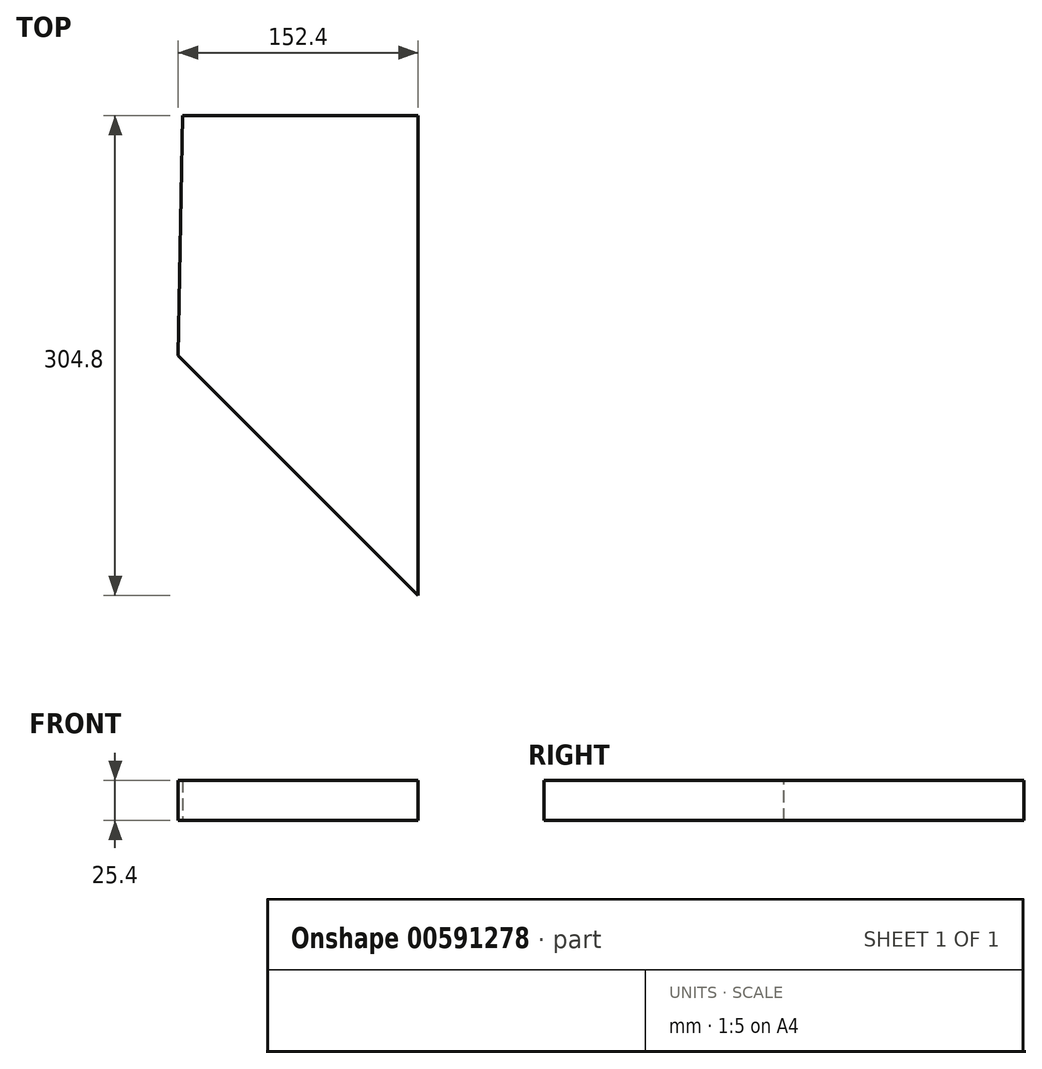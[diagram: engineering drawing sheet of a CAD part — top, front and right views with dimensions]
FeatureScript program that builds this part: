
annotation { "Feature Type Name" : "Feature", "Feature Type Description" : "" }
export const myFeature = defineFeature(function(context is Context, id is Id, definition is map)
    precondition{}
    {
        {
            var Q0;
            Q0=qCreatedBy(makeId("Top.planeOp"),FACE);
            var sketch = newSketch(context, id + "F0", { "sketchPlane" : qUnion([Q0])});
            skLineSegment(sketch, "E0.bottom", {"start": v(152.4, -152.4) * mm, "end": v(-152.4, -152.4) * mm});
            skLineSegment(sketch, "E0.top", {"start": v(152.4, 152.4) * mm, "end": v(-152.4, 152.4) * mm});
            skLineSegment(sketch, "E0.left", {"start": v(152.4, -152.4) * mm, "end": v(152.4, 152.4) * mm});
            skLineSegment(sketch, "E0.right", {"start": v(-152.4, -152.4) * mm, "end": v(-152.4, 152.4) * mm});
            skPoint(sketch, "E0.middle", {"position": v(0, 0) * mm});
            skSolve(sketch);
        }
        {
            var Q0;
            Q0 = qSketchRegion(id + "F0", true);
            extrude(context, id + "F1", {"entities" : qUnion([Q0]), "depth" : 25.4 * mm, "offsetDistance" : 25.4 * mm});
        }
        {
            var Q0;
            Q0=makeQuery(id+"F1.opExtrude","CAP_FACE",FACE,{"disambiguationData":[OSD([sQuery(id+"F0.wireOp",EDGE,"E0.bottom"),sQuery(id+"F0.wireOp",EDGE,"E0.top"),sQuery(id+"F0.wireOp",EDGE,"E0.left"),sQuery(id+"F0.wireOp",EDGE,"E0.right")])],"isStart":false});
            var sketch = newSketch(context, id + "F2", { "sketchPlane" : qUnion([Q0])});
            skLineSegment(sketch, "E1", {"start": v(0, 0) * mm, "end": v(-152.4, 152.4) * mm});
            skLineSegment(sketch, "E2", {"start": v(-152.4, 152.4) * mm, "end": v(0, 0) * mm});
            skLineSegment(sketch, "E3", {"start": v(0, 0) * mm, "end": v(152.4, 152.4) * mm});
            skLineSegment(sketch, "E4", {"start": v(0, 0) * mm, "end": v(-152.4, -152.4) * mm});
            skLineSegment(sketch, "E5", {"start": v(0, 0) * mm, "end": v(152.4, -152.4) * mm});
            skSolve(sketch);
        }
        {
            var Q0;
            Q0=makeQuery(id+"F2.imprint","IMPRINT",FACE,{"disambiguationData":[TD([[makeQuery(id+"F2.imprint","IMPRINT",EDGE,{"derivedFrom":sQuery(id+"F2.wireOp",EDGE,"E4")}),1.0]])]});
            extrude(context, id + "F3", {"entities" : qUnion([Q0]), "operationType" : NewBodyOperationType.REMOVE, "oppositeDirection" : true, "depth" : 25.4 * mm, "offsetDistance" : 25.4 * mm});
        }
        {
            var Q0;
            Q0=makeQuery(id+"F1.opExtrude","CAP_FACE",FACE,{"disambiguationData":[OSD([sQuery(id+"F0.wireOp",EDGE,"E0.bottom"),sQuery(id+"F0.wireOp",EDGE,"E0.top"),sQuery(id+"F0.wireOp",EDGE,"E0.left"),sQuery(id+"F0.wireOp",EDGE,"E0.right")])],"isStart":true});
            var sketch = newSketch(context, id + "F4", { "sketchPlane" : qUnion([Q0])});
            skLineSegment(sketch, "E6", {"start": v(0, 0) * mm, "end": v(2.95, -152.4) * mm});
            skSolve(sketch);
        }
        {
            var Q0;
            {var subQ0=sQuery(id+"F4.wireOp",EDGE,"E6");Q0=makeQuery(id+"F4.imprint","IMPRINT",FACE,{"disambiguationData":[TD([[makeQuery(id+"F4.imprint","IMPRINT",EDGE,{"derivedFrom":subQ0}),-1.0]])]});}
            extrude(context, id + "F5", {"entities" : qUnion([Q0]), "operationType" : NewBodyOperationType.REMOVE, "oppositeDirection" : true, "depth" : 25.4 * mm, "offsetDistance" : 25.4 * mm});
        }
    });
